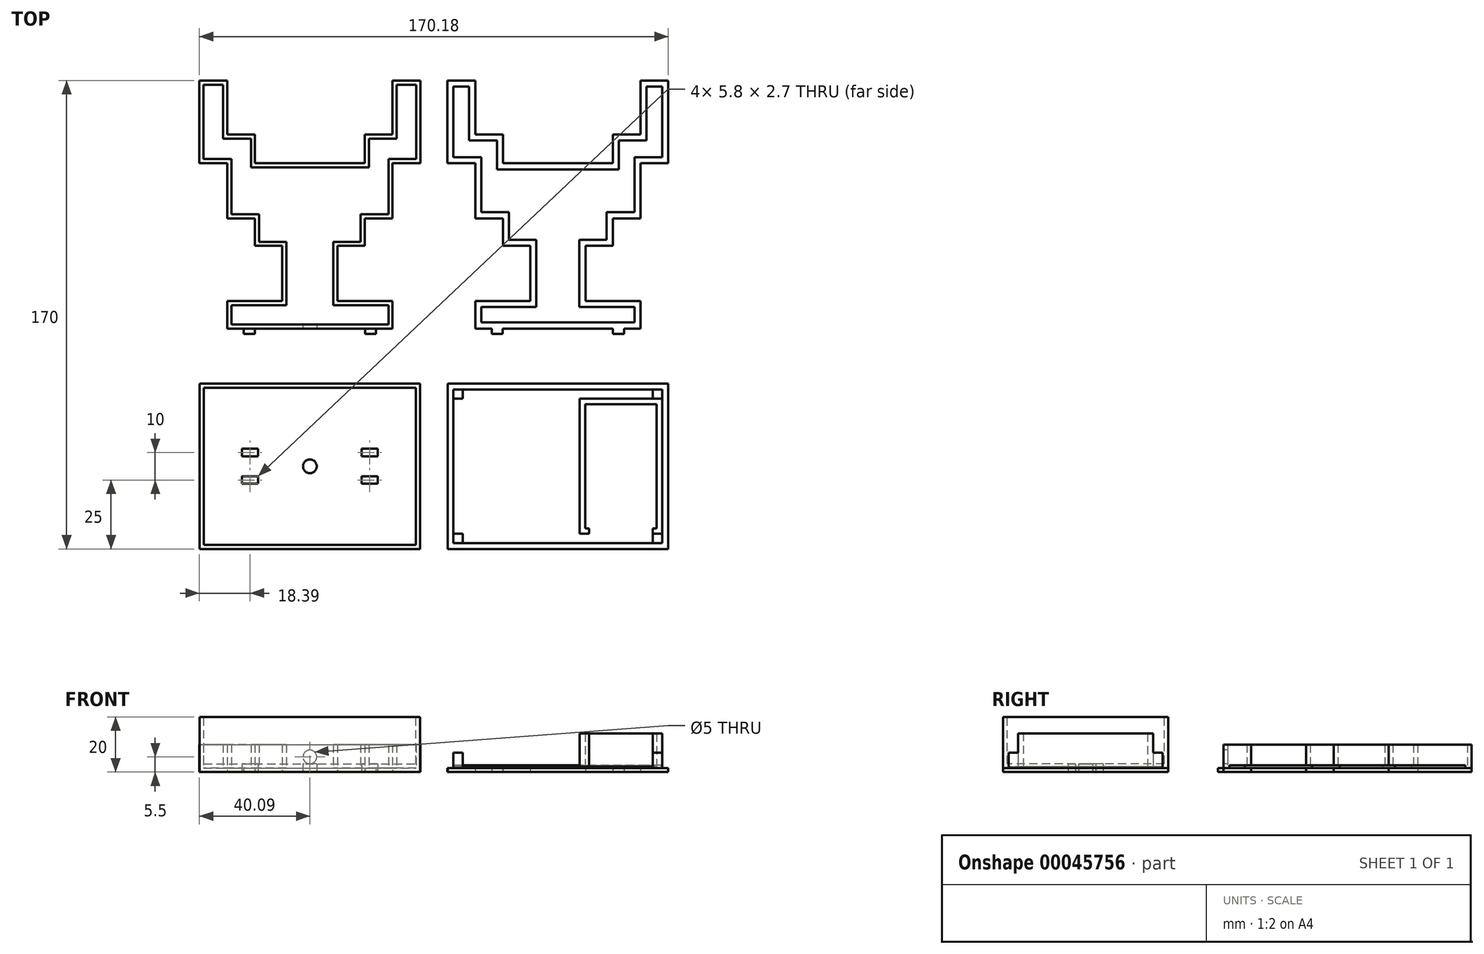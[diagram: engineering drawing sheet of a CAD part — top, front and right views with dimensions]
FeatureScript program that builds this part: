
annotation { "Feature Type Name" : "Feature", "Feature Type Description" : "" }
export const myFeature = defineFeature(function(context is Context, id is Id, definition is map)
    precondition{}
    {
        {
            var Q0;
            Q0=qCreatedBy(makeId("Top.planeOp"),FACE);
            var sketch = newSketch(context, id + "F0", { "sketchPlane" : qUnion([Q0])});
            skLineSegment(sketch, "E0", {"start": v(0, 0) * mm, "end": v(0, 20) * mm, "construction": true});
            skLineSegment(sketch, "E1", {"start": v(0, 0) * mm, "end": v(0, -40) * mm, "construction": true});
            skLineSegment(sketch, "E2", {"start": v(-30, -40) * mm, "end": v(30, -40) * mm});
            skLineSegment(sketch, "E3", {"start": v(-30, -40) * mm, "end": v(-30, -30) * mm});
            skLineSegment(sketch, "E4", {"start": v(-30, -30) * mm, "end": v(-10, -30) * mm});
            skLineSegment(sketch, "E5", {"start": v(-10, -30) * mm, "end": v(-10, -10) * mm});
            skLineSegment(sketch, "E6", {"start": v(-10, -10) * mm, "end": v(-19.9, -10) * mm});
            skLineSegment(sketch, "E7", {"start": v(-19.9, -10) * mm, "end": v(-19.9, 0) * mm});
            skLineSegment(sketch, "E8", {"start": v(-19.9, 0) * mm, "end": v(-30, 0) * mm});
            skLineSegment(sketch, "E9", {"start": v(-19.9, 20) * mm, "end": v(19.9, 20) * mm});
            skLineSegment(sketch, "E10", {"start": v(-19.9, 20) * mm, "end": v(-19.9, 0) * mm, "construction": true});
            skLineSegment(sketch, "E11", {"start": v(-30, 0) * mm, "end": v(-30, 20) * mm});
            skLineSegment(sketch, "E12", {"start": v(-30, 20) * mm, "end": v(-40.1, 20) * mm});
            skLineSegment(sketch, "E13", {"start": v(-40.1, 20) * mm, "end": v(-40.1, 50) * mm});
            skLineSegment(sketch, "E14", {"start": v(-40.1, 50) * mm, "end": v(-30, 50) * mm});
            skLineSegment(sketch, "E15", {"start": v(-30, 50) * mm, "end": v(-30, 30.44) * mm});
            skLineSegment(sketch, "E16", {"start": v(-30, 30.44) * mm, "end": v(-19.9, 30.44) * mm});
            skLineSegment(sketch, "E17", {"start": v(-19.9, 30.44) * mm, "end": v(-19.9, 20) * mm});
            skLineSegment(sketch, "E18.MirrorCS", {"start": v(19.9, 30.44) * mm, "end": v(19.9, 20) * mm});
            skLineSegment(sketch, "E19.MirrorCS", {"start": v(30, 30.44) * mm, "end": v(19.9, 30.44) * mm});
            skLineSegment(sketch, "E20.MirrorCS", {"start": v(30, 50) * mm, "end": v(30, 30.44) * mm});
            skLineSegment(sketch, "E21.MirrorCS", {"start": v(40.1, 50) * mm, "end": v(30, 50) * mm});
            skLineSegment(sketch, "E22.MirrorCS", {"start": v(40.1, 20) * mm, "end": v(40.1, 50) * mm});
            skLineSegment(sketch, "E23.MirrorCS", {"start": v(30, 20) * mm, "end": v(40.1, 20) * mm});
            skLineSegment(sketch, "E24.MirrorCS", {"start": v(30, 0) * mm, "end": v(30, 20) * mm});
            skLineSegment(sketch, "E25.MirrorCS", {"start": v(19.9, 0) * mm, "end": v(30, 0) * mm});
            skLineSegment(sketch, "E26.MirrorCS", {"start": v(19.9, -10) * mm, "end": v(19.9, 0) * mm});
            skLineSegment(sketch, "E27.MirrorCS", {"start": v(10, -10) * mm, "end": v(19.9, -10) * mm});
            skLineSegment(sketch, "E28.MirrorCS", {"start": v(10, -30) * mm, "end": v(10, -10) * mm});
            skLineSegment(sketch, "E29.MirrorCS", {"start": v(30, -30) * mm, "end": v(10, -30) * mm});
            skLineSegment(sketch, "E30.MirrorCS", {"start": v(30, -40) * mm, "end": v(30, -30) * mm});
            skLineSegment(sketch, "E31", {"start": v(0, -42) * mm, "end": v(-20, -42) * mm, "construction": true});
            skLineSegment(sketch, "E32.bottom", {"start": v(-20, -42) * mm, "end": v(-24, -42) * mm});
            skLineSegment(sketch, "E32.top", {"start": v(-20, -40) * mm, "end": v(-24, -40) * mm});
            skLineSegment(sketch, "E32.left", {"start": v(-20, -42) * mm, "end": v(-20, -40) * mm});
            skLineSegment(sketch, "E32.right", {"start": v(-24, -42) * mm, "end": v(-24, -40) * mm});
            skLineSegment(sketch, "E33", {"start": v(0, -40) * mm, "end": v(0, -42) * mm, "construction": true});
            skLineSegment(sketch, "E34.MirrorCS", {"start": v(20, -42) * mm, "end": v(20, -40) * mm});
            skLineSegment(sketch, "E35.MirrorCS", {"start": v(20, -42) * mm, "end": v(24, -42) * mm});
            skLineSegment(sketch, "E36.MirrorCS", {"start": v(24, -42) * mm, "end": v(24, -40) * mm});
            skSolve(sketch);
        }
        {
            var Q0;
            Q0=makeQuery(id+"F0.imprint","IMPRINT",FACE,{"disambiguationData":[TD([[makeQuery(id+"F0.imprint","IMPRINT",EDGE,{"derivedFrom":sQuery(id+"F0.wireOp",EDGE,"E2")}),1.0]])]});
            var Q1;
            Q1=makeQuery(id+"F0.imprint","IMPRINT",FACE,{"disambiguationData":[TD([[makeQuery(id+"F0.imprint","IMPRINT",EDGE,{"derivedFrom":sQuery(id+"F0.wireOp",EDGE,"E32.bottom")}),-1.0]])]});
            var Q2;
            {var subQ1=sQuery(id+"F0.wireOp",EDGE,"E34.MirrorCS");Q2=makeQuery(id+"F0.imprint","IMPRINT",FACE,{"disambiguationData":[TD([[makeQuery(id+"F0.imprint","IMPRINT",EDGE,{"derivedFrom":subQ1}),-1.0]])]});}
            extrude(context, id + "F1", {"entities" : qUnion([Q0, Q1, Q2]), "depth" : 1.5 * mm});
        }
        {
            var Q0;
            Q0=makeQuery(id+"F1.opExtrude","SWEPT_BODY",BODY,{"disambiguationData":[OSD([sQuery(id+"F0.wireOp",EDGE,"E2"),sQuery(id+"F0.wireOp",EDGE,"E3"),sQuery(id+"F0.wireOp",EDGE,"E4"),sQuery(id+"F0.wireOp",EDGE,"E5"),sQuery(id+"F0.wireOp",EDGE,"E6"),sQuery(id+"F0.wireOp",EDGE,"E7"),sQuery(id+"F0.wireOp",EDGE,"E8"),sQuery(id+"F0.wireOp",EDGE,"E9"),sQuery(id+"F0.wireOp",EDGE,"E11"),sQuery(id+"F0.wireOp",EDGE,"E12"),sQuery(id+"F0.wireOp",EDGE,"E13"),sQuery(id+"F0.wireOp",EDGE,"E14"),sQuery(id+"F0.wireOp",EDGE,"E15"),sQuery(id+"F0.wireOp",EDGE,"E16"),sQuery(id+"F0.wireOp",EDGE,"E17"),sQuery(id+"F0.wireOp",EDGE,"E18.MirrorCS"),sQuery(id+"F0.wireOp",EDGE,"E19.MirrorCS"),sQuery(id+"F0.wireOp",EDGE,"E20.MirrorCS"),sQuery(id+"F0.wireOp",EDGE,"E21.MirrorCS"),sQuery(id+"F0.wireOp",EDGE,"E22.MirrorCS"),sQuery(id+"F0.wireOp",EDGE,"E23.MirrorCS"),sQuery(id+"F0.wireOp",EDGE,"E24.MirrorCS"),sQuery(id+"F0.wireOp",EDGE,"E25.MirrorCS"),sQuery(id+"F0.wireOp",EDGE,"E26.MirrorCS"),sQuery(id+"F0.wireOp",EDGE,"E27.MirrorCS"),sQuery(id+"F0.wireOp",EDGE,"E28.MirrorCS"),sQuery(id+"F0.wireOp",EDGE,"E29.MirrorCS"),sQuery(id+"F0.wireOp",EDGE,"E30.MirrorCS")])]});
            transform(context, id + "F2", {"entities" : qUnion([Q0]), "transformType" : TransformType.TRANSLATION_3D, "dx" : 90 * mm, "dy" : 0 * mm, "dz" : 0 * mm, "makeCopy" : true});
        }
        {
            var Q0;
            Q0=makeQuery(id+"F1.opExtrude","CAP_FACE",FACE,{"disambiguationData":[OSD([sQuery(id+"F0.wireOp",EDGE,"E2"),sQuery(id+"F0.wireOp",EDGE,"E3"),sQuery(id+"F0.wireOp",EDGE,"E4"),sQuery(id+"F0.wireOp",EDGE,"E5"),sQuery(id+"F0.wireOp",EDGE,"E6"),sQuery(id+"F0.wireOp",EDGE,"E7"),sQuery(id+"F0.wireOp",EDGE,"E8"),sQuery(id+"F0.wireOp",EDGE,"E9"),sQuery(id+"F0.wireOp",EDGE,"E11"),sQuery(id+"F0.wireOp",EDGE,"E12"),sQuery(id+"F0.wireOp",EDGE,"E13"),sQuery(id+"F0.wireOp",EDGE,"E14"),sQuery(id+"F0.wireOp",EDGE,"E15"),sQuery(id+"F0.wireOp",EDGE,"E16"),sQuery(id+"F0.wireOp",EDGE,"E17"),sQuery(id+"F0.wireOp",EDGE,"E18.MirrorCS"),sQuery(id+"F0.wireOp",EDGE,"E19.MirrorCS"),sQuery(id+"F0.wireOp",EDGE,"E20.MirrorCS"),sQuery(id+"F0.wireOp",EDGE,"E21.MirrorCS"),sQuery(id+"F0.wireOp",EDGE,"E22.MirrorCS"),sQuery(id+"F0.wireOp",EDGE,"E23.MirrorCS"),sQuery(id+"F0.wireOp",EDGE,"E24.MirrorCS"),sQuery(id+"F0.wireOp",EDGE,"E25.MirrorCS"),sQuery(id+"F0.wireOp",EDGE,"E26.MirrorCS"),sQuery(id+"F0.wireOp",EDGE,"E27.MirrorCS"),sQuery(id+"F0.wireOp",EDGE,"E28.MirrorCS"),sQuery(id+"F0.wireOp",EDGE,"E29.MirrorCS"),sQuery(id+"F0.wireOp",EDGE,"E30.MirrorCS"),sQuery(id+"F0.wireOp",EDGE,"E32.bottom"),sQuery(id+"F0.wireOp",EDGE,"E32.left"),sQuery(id+"F0.wireOp",EDGE,"E32.right"),sQuery(id+"F0.wireOp",EDGE,"E34.MirrorCS"),sQuery(id+"F0.wireOp",EDGE,"E35.MirrorCS"),sQuery(id+"F0.wireOp",EDGE,"E36.MirrorCS")])],"isStart":false});
            var sketch = newSketch(context, id + "F3", { "sketchPlane" : qUnion([Q0])});
            skLineSegment(sketch, "E37.0", {"start": v(-30, -40) * mm, "end": v(-30, -30) * mm});
            skLineSegment(sketch, "E38.0", {"start": v(-30, -30) * mm, "end": v(-10, -30) * mm});
            skLineSegment(sketch, "E39.0", {"start": v(-10, -30) * mm, "end": v(-10, -10) * mm});
            skLineSegment(sketch, "E40.0", {"start": v(-10, -10) * mm, "end": v(-19.9, -10) * mm});
            skLineSegment(sketch, "E41.0", {"start": v(-19.9, -10) * mm, "end": v(-19.9, 0) * mm});
            skLineSegment(sketch, "E42.0", {"start": v(-19.9, 0) * mm, "end": v(-30, 0) * mm});
            skLineSegment(sketch, "E43.0", {"start": v(-30, 0) * mm, "end": v(-30, 20) * mm});
            skLineSegment(sketch, "E44.0", {"start": v(-30, 20) * mm, "end": v(-40.1, 20) * mm});
            skLineSegment(sketch, "E45.0", {"start": v(-40.1, 20) * mm, "end": v(-40.1, 50) * mm});
            skLineSegment(sketch, "E46.0", {"start": v(-40.1, 50) * mm, "end": v(-30, 50) * mm});
            skLineSegment(sketch, "E47.0", {"start": v(-30, 50) * mm, "end": v(-30, 30.44) * mm});
            skLineSegment(sketch, "E48.0", {"start": v(-30, 30.44) * mm, "end": v(-19.9, 30.44) * mm});
            skLineSegment(sketch, "E49.0", {"start": v(-19.9, 30.44) * mm, "end": v(-19.9, 20) * mm});
            skLineSegment(sketch, "E50.0", {"start": v(-19.9, 20) * mm, "end": v(19.9, 20) * mm});
            skLineSegment(sketch, "E51.0", {"start": v(19.9, 30.44) * mm, "end": v(19.9, 20) * mm});
            skLineSegment(sketch, "E52.0", {"start": v(30, 30.44) * mm, "end": v(19.9, 30.44) * mm});
            skLineSegment(sketch, "E53.0", {"start": v(30, 50) * mm, "end": v(30, 30.44) * mm});
            skLineSegment(sketch, "E54.0", {"start": v(40.1, 50) * mm, "end": v(30, 50) * mm});
            skLineSegment(sketch, "E55.0", {"start": v(40.1, 20) * mm, "end": v(40.1, 50) * mm});
            skLineSegment(sketch, "E56.0", {"start": v(30, 20) * mm, "end": v(40.1, 20) * mm});
            skLineSegment(sketch, "E57.0", {"start": v(30, 0) * mm, "end": v(30, 20) * mm});
            skLineSegment(sketch, "E58.0", {"start": v(19.9, 0) * mm, "end": v(30, 0) * mm});
            skLineSegment(sketch, "E59.0", {"start": v(19.9, -10) * mm, "end": v(19.9, 0) * mm});
            skLineSegment(sketch, "E60.0", {"start": v(10, -10) * mm, "end": v(19.9, -10) * mm});
            skLineSegment(sketch, "E61.0", {"start": v(10, -30) * mm, "end": v(10, -10) * mm});
            skLineSegment(sketch, "E62.0", {"start": v(30, -30) * mm, "end": v(10, -30) * mm});
            skLineSegment(sketch, "E63.0", {"start": v(30, -40) * mm, "end": v(30, -30) * mm});
            skLineSegment(sketch, "E64", {"start": v(-30, -40) * mm, "end": v(30, -40) * mm});
            skSolve(sketch);
        }
        {
            var Q0;
            {var subQ5=sQuery(id+"F3.wireOp",EDGE,"E37.0");Q0=makeQuery(id+"F3.imprint","IMPRINT",FACE,{"disambiguationData":[TD([[makeQuery(id+"F3.imprint","IMPRINT",EDGE,{"derivedFrom":subQ5}),-1.0]])]});}
            extrude(context, id + "F4", {"entities" : qUnion([Q0]), "operationType" : NewBodyOperationType.ADD, "depth" : 8.5 * mm});
        }
        {
            var Q0;
            Q0=makeQuery(id+"F4.opExtrude","CAP_FACE",FACE,{"disambiguationData":[OSD([sQuery(id+"F3.wireOp",EDGE,"E37.0"),sQuery(id+"F3.wireOp",EDGE,"E38.0"),sQuery(id+"F3.wireOp",EDGE,"E39.0"),sQuery(id+"F3.wireOp",EDGE,"E40.0"),sQuery(id+"F3.wireOp",EDGE,"E41.0"),sQuery(id+"F3.wireOp",EDGE,"E42.0"),sQuery(id+"F3.wireOp",EDGE,"E43.0"),sQuery(id+"F3.wireOp",EDGE,"E44.0"),sQuery(id+"F3.wireOp",EDGE,"E45.0"),sQuery(id+"F3.wireOp",EDGE,"E46.0"),sQuery(id+"F3.wireOp",EDGE,"E47.0"),sQuery(id+"F3.wireOp",EDGE,"E48.0"),sQuery(id+"F3.wireOp",EDGE,"E49.0"),sQuery(id+"F3.wireOp",EDGE,"E50.0"),sQuery(id+"F3.wireOp",EDGE,"E51.0"),sQuery(id+"F3.wireOp",EDGE,"E52.0"),sQuery(id+"F3.wireOp",EDGE,"E53.0"),sQuery(id+"F3.wireOp",EDGE,"E54.0"),sQuery(id+"F3.wireOp",EDGE,"E55.0"),sQuery(id+"F3.wireOp",EDGE,"E56.0"),sQuery(id+"F3.wireOp",EDGE,"E57.0"),sQuery(id+"F3.wireOp",EDGE,"E58.0"),sQuery(id+"F3.wireOp",EDGE,"E59.0"),sQuery(id+"F3.wireOp",EDGE,"E60.0"),sQuery(id+"F3.wireOp",EDGE,"E61.0"),sQuery(id+"F3.wireOp",EDGE,"E62.0"),sQuery(id+"F3.wireOp",EDGE,"E63.0"),sQuery(id+"F3.wireOp",EDGE,"E64")])],"isStart":false});
            shell(context, id + "F5", {"entities" : qUnion([Q0]), "thickness" : 1.5 * mm});
        }
        {
            var Q0;
            {var subQ0=sQuery(id+"F0.wireOp",EDGE,"E2");Q0=makeQuery(id+"F4.boolean.opBoolean","MERGE",FACE,{"derivedFrom":[makeQuery(id+"F1.opExtrude","SWEPT_FACE",FACE,{"disambiguationData":[OSD([subQ0])]}),makeQuery(id+"F4.opExtrude","SWEPT_FACE",FACE,{"disambiguationData":[OSD([subQ0])]})]});}
            var sketch = newSketch(context, id + "F6", { "sketchPlane" : qUnion([Q0])});
            skLineSegment(sketch, "E65", {"start": v(0, 0) * mm, "end": v(0, 5.5) * mm, "construction": true});
            skLineSegment(sketch, "E66.0", {"start": v(-20, 0) * mm, "end": v(20, 0) * mm, "construction": true});
            skPoint(sketch, "E67", {"position": v(0, 5.5) * mm});
            skSolve(sketch);
        }
        {
            var Q0;
            Q0=sQuery(id+"F6.wireOp",VERTEX,"E67");
            var Q1;
            Q1=makeQuery(id+"F1.opExtrude","SWEPT_BODY",BODY,{"disambiguationData":[OSD([sQuery(id+"F0.wireOp",EDGE,"E2"),sQuery(id+"F0.wireOp",EDGE,"E3"),sQuery(id+"F0.wireOp",EDGE,"E4"),sQuery(id+"F0.wireOp",EDGE,"E5"),sQuery(id+"F0.wireOp",EDGE,"E6"),sQuery(id+"F0.wireOp",EDGE,"E7"),sQuery(id+"F0.wireOp",EDGE,"E8"),sQuery(id+"F0.wireOp",EDGE,"E9"),sQuery(id+"F0.wireOp",EDGE,"E11"),sQuery(id+"F0.wireOp",EDGE,"E12"),sQuery(id+"F0.wireOp",EDGE,"E13"),sQuery(id+"F0.wireOp",EDGE,"E14"),sQuery(id+"F0.wireOp",EDGE,"E15"),sQuery(id+"F0.wireOp",EDGE,"E16"),sQuery(id+"F0.wireOp",EDGE,"E17"),sQuery(id+"F0.wireOp",EDGE,"E18.MirrorCS"),sQuery(id+"F0.wireOp",EDGE,"E19.MirrorCS"),sQuery(id+"F0.wireOp",EDGE,"E20.MirrorCS"),sQuery(id+"F0.wireOp",EDGE,"E21.MirrorCS"),sQuery(id+"F0.wireOp",EDGE,"E22.MirrorCS"),sQuery(id+"F0.wireOp",EDGE,"E23.MirrorCS"),sQuery(id+"F0.wireOp",EDGE,"E24.MirrorCS"),sQuery(id+"F0.wireOp",EDGE,"E25.MirrorCS"),sQuery(id+"F0.wireOp",EDGE,"E26.MirrorCS"),sQuery(id+"F0.wireOp",EDGE,"E27.MirrorCS"),sQuery(id+"F0.wireOp",EDGE,"E28.MirrorCS"),sQuery(id+"F0.wireOp",EDGE,"E29.MirrorCS"),sQuery(id+"F0.wireOp",EDGE,"E30.MirrorCS")])]});
            hole(context, id + "F7", {"style" : HoleStyle.SIMPLE, "holeDiameter" : 5 * mm, "endStyle" : HoleEndStyle.BLIND, "holeDepth" : 20 * mm, "locations" : qUnion([Q0]), "scope" : qUnion([Q1])});
        }
        {
            var Q0;
            Q0=makeQuery(id+"F2.opPattern","COPY",FACE,{"derivedFrom":makeQuery(id+"F1.opExtrude","CAP_FACE",FACE,{"disambiguationData":[OSD([sQuery(id+"F0.wireOp",EDGE,"E2"),sQuery(id+"F0.wireOp",EDGE,"E3"),sQuery(id+"F0.wireOp",EDGE,"E4"),sQuery(id+"F0.wireOp",EDGE,"E5"),sQuery(id+"F0.wireOp",EDGE,"E6"),sQuery(id+"F0.wireOp",EDGE,"E7"),sQuery(id+"F0.wireOp",EDGE,"E8"),sQuery(id+"F0.wireOp",EDGE,"E9"),sQuery(id+"F0.wireOp",EDGE,"E11"),sQuery(id+"F0.wireOp",EDGE,"E12"),sQuery(id+"F0.wireOp",EDGE,"E13"),sQuery(id+"F0.wireOp",EDGE,"E14"),sQuery(id+"F0.wireOp",EDGE,"E15"),sQuery(id+"F0.wireOp",EDGE,"E16"),sQuery(id+"F0.wireOp",EDGE,"E17"),sQuery(id+"F0.wireOp",EDGE,"E18.MirrorCS"),sQuery(id+"F0.wireOp",EDGE,"E19.MirrorCS"),sQuery(id+"F0.wireOp",EDGE,"E20.MirrorCS"),sQuery(id+"F0.wireOp",EDGE,"E21.MirrorCS"),sQuery(id+"F0.wireOp",EDGE,"E22.MirrorCS"),sQuery(id+"F0.wireOp",EDGE,"E23.MirrorCS"),sQuery(id+"F0.wireOp",EDGE,"E24.MirrorCS"),sQuery(id+"F0.wireOp",EDGE,"E25.MirrorCS"),sQuery(id+"F0.wireOp",EDGE,"E26.MirrorCS"),sQuery(id+"F0.wireOp",EDGE,"E27.MirrorCS"),sQuery(id+"F0.wireOp",EDGE,"E28.MirrorCS"),sQuery(id+"F0.wireOp",EDGE,"E29.MirrorCS"),sQuery(id+"F0.wireOp",EDGE,"E30.MirrorCS")])],"isStart":false}),"instanceName":"1"});
            var sketch = newSketch(context, id + "F8", { "sketchPlane" : qUnion([Q0])});
            skLineSegment(sketch, "E68.0", {"start": v(62.2, -37.8) * mm, "end": v(62.2, -32.2) * mm});
            skLineSegment(sketch, "E68.1", {"start": v(62.2, -32.2) * mm, "end": v(82.2, -32.2) * mm});
            skLineSegment(sketch, "E68.2", {"start": v(82.2, -32.2) * mm, "end": v(82.2, -7.8) * mm});
            skLineSegment(sketch, "E68.3", {"start": v(82.2, -7.8) * mm, "end": v(72.3, -7.8) * mm});
            skLineSegment(sketch, "E68.4", {"start": v(72.3, -7.8) * mm, "end": v(72.3, 2.2) * mm});
            skLineSegment(sketch, "E68.5", {"start": v(127.9, 47.8) * mm, "end": v(122.2, 47.8) * mm});
            skLineSegment(sketch, "E68.6", {"start": v(127.9, 22.2) * mm, "end": v(127.9, 47.8) * mm});
            skLineSegment(sketch, "E68.7", {"start": v(117.8, 22.2) * mm, "end": v(127.9, 22.2) * mm});
            skLineSegment(sketch, "E68.8", {"start": v(117.8, 2.2) * mm, "end": v(117.8, 22.2) * mm});
            skLineSegment(sketch, "E68.9", {"start": v(107.7, 2.2) * mm, "end": v(117.8, 2.2) * mm});
            skLineSegment(sketch, "E68.10", {"start": v(107.7, -7.8) * mm, "end": v(107.7, 2.2) * mm});
            skLineSegment(sketch, "E68.11", {"start": v(117.8, -37.8) * mm, "end": v(117.8, -32.2) * mm});
            skLineSegment(sketch, "E68.12", {"start": v(117.8, -32.2) * mm, "end": v(97.8, -32.2) * mm});
            skLineSegment(sketch, "E68.13", {"start": v(97.8, -32.2) * mm, "end": v(97.8, -7.8) * mm});
            skLineSegment(sketch, "E68.14", {"start": v(97.8, -7.8) * mm, "end": v(107.7, -7.8) * mm});
            skLineSegment(sketch, "E68.15", {"start": v(122.2, 47.8) * mm, "end": v(122.2, 28.24) * mm});
            skLineSegment(sketch, "E68.16", {"start": v(122.2, 28.24) * mm, "end": v(112.1, 28.24) * mm});
            skLineSegment(sketch, "E68.17", {"start": v(112.1, 28.24) * mm, "end": v(112.1, 17.8) * mm});
            skLineSegment(sketch, "E68.18", {"start": v(67.9, 17.8) * mm, "end": v(112.1, 17.8) * mm});
            skLineSegment(sketch, "E68.19", {"start": v(67.9, 28.24) * mm, "end": v(67.9, 17.8) * mm});
            skLineSegment(sketch, "E68.20", {"start": v(62.2, -37.8) * mm, "end": v(117.8, -37.8) * mm});
            skLineSegment(sketch, "E68.21", {"start": v(57.8, 28.24) * mm, "end": v(67.9, 28.24) * mm});
            skLineSegment(sketch, "E68.22", {"start": v(57.8, 47.8) * mm, "end": v(57.8, 28.24) * mm});
            skLineSegment(sketch, "E68.23", {"start": v(52.1, 47.8) * mm, "end": v(57.8, 47.8) * mm});
            skLineSegment(sketch, "E68.24", {"start": v(52.1, 22.2) * mm, "end": v(52.1, 47.8) * mm});
            skLineSegment(sketch, "E68.25", {"start": v(62.2, 22.2) * mm, "end": v(52.1, 22.2) * mm});
            skLineSegment(sketch, "E68.26", {"start": v(62.2, 2.2) * mm, "end": v(62.2, 22.2) * mm});
            skLineSegment(sketch, "E68.27", {"start": v(72.3, 2.2) * mm, "end": v(62.2, 2.2) * mm});
            skSolve(sketch);
        }
        {
            var Q0;
            Q0 = qSketchRegion(id + "F8", true);
            extrude(context, id + "F9", {"entities" : qUnion([Q0]), "operationType" : NewBodyOperationType.ADD, "depth" : 1 * mm});
        }
        {
            var Q0;
            Q0=qCreatedBy(makeId("Top.planeOp"),FACE);
            var sketch = newSketch(context, id + "F10", { "sketchPlane" : qUnion([Q0])});
            skLineSegment(sketch, "E69", {"start": v(0, 0) * mm, "end": v(0, -90) * mm, "construction": true});
            skLineSegment(sketch, "E70.rect.bottom", {"start": v(-40, -60) * mm, "end": v(40, -60) * mm});
            skLineSegment(sketch, "E70.rect.top", {"start": v(-40, -120) * mm, "end": v(40, -120) * mm});
            skLineSegment(sketch, "E70.rect.left", {"start": v(-40, -60) * mm, "end": v(-40, -120) * mm});
            skLineSegment(sketch, "E70.rect.right", {"start": v(40, -60) * mm, "end": v(40, -120) * mm});
            skPoint(sketch, "E70.rect.middle", {"position": v(0, -90) * mm});
            skCircle(sketch, "E71", {"center": v(0, -90) * mm, "radius": 2.5 * mm});
            skPoint(sketch, "E72.0", {"position": v(-20, -42) * mm});
            skPoint(sketch, "E73.0", {"position": v(-24, -42) * mm});
            skLineSegment(sketch, "E74", {"start": v(-19.4, -85.75) * mm, "end": v(-24, -85.75) * mm, "construction": true});
            skLineSegment(sketch, "E75", {"start": v(-24, -85.75) * mm, "end": v(-24, -84.25) * mm, "construction": true});
            skLineSegment(sketch, "E76", {"start": v(-24, -84.25) * mm, "end": v(-19.4, -84.25) * mm, "construction": true});
            skLineSegment(sketch, "E77", {"start": v(-19.4, -84.25) * mm, "end": v(-19.4, -85.75) * mm, "construction": true});
            skLineSegment(sketch, "E78.0", {"start": v(-24.6, -83.65) * mm, "end": v(-18.8, -83.65) * mm});
            skLineSegment(sketch, "E78.1", {"start": v(-24.6, -86.35) * mm, "end": v(-24.6, -83.65) * mm});
            skLineSegment(sketch, "E78.2", {"start": v(-18.8, -86.35) * mm, "end": v(-24.6, -86.35) * mm});
            skLineSegment(sketch, "E78.3", {"start": v(-18.8, -83.65) * mm, "end": v(-18.8, -86.35) * mm});
            skLineSegment(sketch, "E79", {"start": v(0, -90) * mm, "end": v(-21.7, -90) * mm, "construction": true});
            skLineSegment(sketch, "E80", {"start": v(-21.7, -90) * mm, "end": v(-21.7, -85.75) * mm, "construction": true});
            skLineSegment(sketch, "E81.MirrorCS", {"start": v(-18.8, -93.65) * mm, "end": v(-24.6, -93.65) * mm});
            skLineSegment(sketch, "E82.MirrorCS", {"start": v(-18.8, -96.35) * mm, "end": v(-18.8, -93.65) * mm});
            skLineSegment(sketch, "E83.MirrorCS", {"start": v(-24.6, -96.35) * mm, "end": v(-18.8, -96.35) * mm});
            skLineSegment(sketch, "E84.MirrorCS", {"start": v(-24.6, -93.65) * mm, "end": v(-24.6, -96.35) * mm});
            skLineSegment(sketch, "E85.MirrorCS", {"start": v(18.8, -83.65) * mm, "end": v(18.8, -86.35) * mm});
            skLineSegment(sketch, "E86.MirrorCS", {"start": v(24.6, -83.65) * mm, "end": v(18.8, -83.65) * mm});
            skLineSegment(sketch, "E87.MirrorCS", {"start": v(24.6, -86.35) * mm, "end": v(24.6, -83.65) * mm});
            skLineSegment(sketch, "E88.MirrorCS", {"start": v(18.8, -86.35) * mm, "end": v(24.6, -86.35) * mm});
            skLineSegment(sketch, "E89.MirrorCS", {"start": v(24.6, -93.65) * mm, "end": v(24.6, -96.35) * mm});
            skLineSegment(sketch, "E90.MirrorCS", {"start": v(18.8, -96.35) * mm, "end": v(18.8, -93.65) * mm});
            skLineSegment(sketch, "E91.MirrorCS", {"start": v(18.8, -93.65) * mm, "end": v(24.6, -93.65) * mm});
            skLineSegment(sketch, "E92.MirrorCS", {"start": v(24.6, -96.35) * mm, "end": v(18.8, -96.35) * mm});
            skSolve(sketch);
        }
        {
            var Q0;
            Q0=makeQuery(id+"F10.imprint","IMPRINT",FACE,{"disambiguationData":[TD([[makeQuery(id+"F10.imprint","IMPRINT",EDGE,{"derivedFrom":sQuery(id+"F10.wireOp",EDGE,"E70.rect.bottom")}),-1.0]])]});
            extrude(context, id + "F11", {"entities" : qUnion([Q0]), "depth" : 20 * mm});
        }
        {
            var Q0;
            Q0=makeQuery(id+"F11.opExtrude","CAP_FACE",FACE,{"disambiguationData":[OSD([sQuery(id+"F10.wireOp",EDGE,"E70.rect.bottom"),sQuery(id+"F10.wireOp",EDGE,"E70.rect.top"),sQuery(id+"F10.wireOp",EDGE,"E70.rect.left"),sQuery(id+"F10.wireOp",EDGE,"E70.rect.right"),sQuery(id+"F10.wireOp",EDGE,"E71"),sQuery(id+"F10.wireOp",EDGE,"E78.0"),sQuery(id+"F10.wireOp",EDGE,"E78.1"),sQuery(id+"F10.wireOp",EDGE,"E78.2"),sQuery(id+"F10.wireOp",EDGE,"E78.3"),sQuery(id+"F10.wireOp",EDGE,"E81.MirrorCS"),sQuery(id+"F10.wireOp",EDGE,"E82.MirrorCS"),sQuery(id+"F10.wireOp",EDGE,"E83.MirrorCS"),sQuery(id+"F10.wireOp",EDGE,"E84.MirrorCS"),sQuery(id+"F10.wireOp",EDGE,"E85.MirrorCS"),sQuery(id+"F10.wireOp",EDGE,"E86.MirrorCS"),sQuery(id+"F10.wireOp",EDGE,"E87.MirrorCS"),sQuery(id+"F10.wireOp",EDGE,"E88.MirrorCS"),sQuery(id+"F10.wireOp",EDGE,"E89.MirrorCS"),sQuery(id+"F10.wireOp",EDGE,"E90.MirrorCS"),sQuery(id+"F10.wireOp",EDGE,"E91.MirrorCS"),sQuery(id+"F10.wireOp",EDGE,"E92.MirrorCS")])],"isStart":false});
            var sketch = newSketch(context, id + "F12", { "sketchPlane" : qUnion([Q0])});
            skLineSegment(sketch, "E93.0", {"start": v(-38.5, -61.5) * mm, "end": v(-38.5, -118.5) * mm});
            skLineSegment(sketch, "E93.1", {"start": v(-38.5, -61.5) * mm, "end": v(38.5, -61.5) * mm});
            skLineSegment(sketch, "E93.2", {"start": v(38.5, -61.5) * mm, "end": v(38.5, -118.5) * mm});
            skLineSegment(sketch, "E93.3", {"start": v(-38.5, -118.5) * mm, "end": v(38.5, -118.5) * mm});
            skSolve(sketch);
        }
        {
            var Q0;
            Q0 = qSketchRegion(id + "F12", true);
            extrude(context, id + "F13", {"entities" : qUnion([Q0]), "operationType" : NewBodyOperationType.REMOVE, "oppositeDirection" : true, "depth" : 18.5 * mm});
        }
        {
            var Q0;
            Q0=qCreatedBy(makeId("Top.planeOp"),FACE);
            var sketch = newSketch(context, id + "F14", { "sketchPlane" : qUnion([Q0])});
            skCircle(sketch, "E94.0", {"center": v(0, -90) * mm, "radius": 2.5 * mm, "construction": true});
            skLineSegment(sketch, "E95", {"start": v(0, -90) * mm, "end": v(90, -90) * mm, "construction": true});
            skLineSegment(sketch, "E96.rect.bottom", {"start": v(50, -60) * mm, "end": v(130, -60) * mm});
            skLineSegment(sketch, "E96.rect.top", {"start": v(50, -120) * mm, "end": v(130, -120) * mm});
            skLineSegment(sketch, "E96.rect.left", {"start": v(50, -60) * mm, "end": v(50, -120) * mm});
            skLineSegment(sketch, "E96.rect.right", {"start": v(130, -60) * mm, "end": v(130, -120) * mm});
            skPoint(sketch, "E96.rect.middle", {"position": v(90, -90) * mm});
            skSolve(sketch);
        }
        {
            var Q0;
            {var subQ0=sQuery(id+"F12.wireOp",EDGE,"E93.0");var subQ1=sQuery(id+"F12.wireOp",EDGE,"E93.1");var subQ2=sQuery(id+"F12.wireOp",EDGE,"E93.2");var subQ3=sQuery(id+"F12.wireOp",EDGE,"E93.3");Q0=makeQuery(id+"FpH8dFIfhSpq4S0_2.boolean.opBoolean","SPLIT",FACE,{"disambiguationData":[TD([makeQuery(id+"F11.opExtrude","SWEPT_FACE",FACE,{"disambiguationData":[OSD([sQuery(id+"F10.wireOp",EDGE,"E71")])]})])],"derivedFrom":makeQuery(id+"F13.boolean.opBoolean","COPY",FACE,{"derivedFrom":makeQuery(id+"F13.opExtrude","CAP_FACE",FACE,{"disambiguationData":[OSD([subQ0,subQ1,subQ2,subQ3])],"isStart":false})})});}
            var Q1;
            Q1=makeQuery(id+"F14.imprint","IMPRINT",FACE,{"disambiguationData":[TD([[makeQuery(id+"F14.imprint","IMPRINT",EDGE,{"derivedFrom":sQuery(id+"F14.wireOp",EDGE,"E96.rect.bottom")}),-1.0]])]});
            extrude(context, id + "F15", {"entities" : qUnion([Q0, Q1]), "operationType" : NewBodyOperationType.ADD, "depth" : 1.5 * mm});
        }
        {
            var Q0;
            Q0=makeQuery(id+"F15.opExtrude","CAP_FACE",FACE,{"disambiguationData":[OSD([sQuery(id+"F14.wireOp",EDGE,"E96.rect.bottom"),sQuery(id+"F14.wireOp",EDGE,"E96.rect.top"),sQuery(id+"F14.wireOp",EDGE,"E96.rect.left"),sQuery(id+"F14.wireOp",EDGE,"E96.rect.right")])],"isStart":false});
            var sketch = newSketch(context, id + "F16", { "sketchPlane" : qUnion([Q0])});
            skLineSegment(sketch, "E97.0", {"start": v(52.1, -62.1) * mm, "end": v(127.9, -62.1) * mm});
            skLineSegment(sketch, "E97.1", {"start": v(52.1, -62.1) * mm, "end": v(52.1, -117.9) * mm});
            skLineSegment(sketch, "E97.2", {"start": v(52.1, -117.9) * mm, "end": v(127.9, -117.9) * mm});
            skLineSegment(sketch, "E97.3", {"start": v(127.9, -62.1) * mm, "end": v(127.9, -117.9) * mm});
            skSolve(sketch);
        }
        {
            var Q0;
            Q0 = qSketchRegion(id + "F16", true);
            extrude(context, id + "F17", {"entities" : qUnion([Q0]), "operationType" : NewBodyOperationType.ADD, "depth" : .5 * mm});
        }
        {
            var Q0;
            Q0=makeQuery(id+"F17.opExtrude","CAP_FACE",FACE,{"disambiguationData":[OSD([sQuery(id+"F16.wireOp",EDGE,"E97.0"),sQuery(id+"F16.wireOp",EDGE,"E97.1"),sQuery(id+"F16.wireOp",EDGE,"E97.2"),sQuery(id+"F16.wireOp",EDGE,"E97.3")])],"isStart":false});
            var sketch = newSketch(context, id + "F18", { "sketchPlane" : qUnion([Q0])});
            skLineSegment(sketch, "E98.0", {"start": v(127.9, -62.1) * mm, "end": v(127.9, -117.9) * mm, "construction": true});
            skLineSegment(sketch, "E99.bottom", {"start": v(97.9, -65.5) * mm, "end": v(127.9, -65.5) * mm});
            skLineSegment(sketch, "E99.top", {"start": v(97.9, -114.5) * mm, "end": v(127.9, -114.5) * mm});
            skLineSegment(sketch, "E99.left", {"start": v(97.9, -65.5) * mm, "end": v(97.9, -114.5) * mm});
            skLineSegment(sketch, "E99.right", {"start": v(127.9, -65.5) * mm, "end": v(127.9, -114.5) * mm});
            skPoint(sketch, "E100", {"position": v(127.9, -90) * mm});
            skLineSegment(sketch, "E101.0", {"start": v(99.9, -67.5) * mm, "end": v(125.9, -67.5) * mm});
            skLineSegment(sketch, "E101.1", {"start": v(99.9, -67.5) * mm, "end": v(99.9, -112.5) * mm});
            skLineSegment(sketch, "E101.2", {"start": v(99.9, -112.5) * mm, "end": v(125.9, -112.5) * mm});
            skLineSegment(sketch, "E101.3", {"start": v(125.9, -67.5) * mm, "end": v(125.9, -112.5) * mm});
            skPoint(sketch, "E102.endSnap0", {"position": v(90, -117.9) * mm});
            skSolve(sketch);
        }
        {
            var Q0;
            Q0 = qSketchRegion(id + "F18", true);
            extrude(context, id + "F19", {"entities" : qUnion([Q0]), "operationType" : NewBodyOperationType.ADD, "depth" : 12 * mm});
        }
        {
            var Q0;
            {var subQ0=sQuery(id+"F16.wireOp",EDGE,"E97.0");var subQ1=sQuery(id+"F16.wireOp",EDGE,"E97.1");var subQ2=sQuery(id+"F16.wireOp",EDGE,"E97.2");var subQ3=sQuery(id+"F16.wireOp",EDGE,"E97.3");Q0=makeQuery(id+"F19.boolean.opBoolean","SPLIT",FACE,{"disambiguationData":[TD([makeQuery(id+"F17.opExtrude","SWEPT_FACE",FACE,{"disambiguationData":[OSD([subQ0])]})])],"derivedFrom":makeQuery(id+"F17.opExtrude","CAP_FACE",FACE,{"disambiguationData":[OSD([subQ0,subQ1,subQ2,subQ3])],"isStart":false})});}
            var sketch = newSketch(context, id + "F20", { "sketchPlane" : qUnion([Q0])});
            skLineSegment(sketch, "E103.bottom", {"start": v(127.9, -117.9) * mm, "end": v(124.5, -117.9) * mm});
            skLineSegment(sketch, "E103.top", {"start": v(127.9, -114.5) * mm, "end": v(124.5, -114.5) * mm});
            skLineSegment(sketch, "E103.left", {"start": v(127.9, -117.9) * mm, "end": v(127.9, -114.5) * mm});
            skLineSegment(sketch, "E103.right", {"start": v(124.5, -117.9) * mm, "end": v(124.5, -114.5) * mm});
            skLineSegment(sketch, "E104", {"start": v(90, -62.1) * mm, "end": v(90, -90) * mm, "construction": true});
            skLineSegment(sketch, "E105", {"start": v(90, -90) * mm, "end": v(52.1, -90) * mm, "construction": true});
            skPoint(sketch, "E105.endSnap0", {"position": v(52.1, -90) * mm});
            skLineSegment(sketch, "E106.MirrorCS", {"start": v(124.5, -62.1) * mm, "end": v(124.5, -65.5) * mm});
            skLineSegment(sketch, "E107.MirrorCS", {"start": v(127.9, -65.5) * mm, "end": v(124.5, -65.5) * mm});
            skLineSegment(sketch, "E108.MirrorCS", {"start": v(127.9, -62.1) * mm, "end": v(127.9, -65.5) * mm});
            skLineSegment(sketch, "E109.MirrorCS", {"start": v(127.9, -62.1) * mm, "end": v(124.5, -62.1) * mm});
            skLineSegment(sketch, "E110.MirrorCS", {"start": v(52.1, -65.5) * mm, "end": v(55.5, -65.5) * mm});
            skLineSegment(sketch, "E111.MirrorCS", {"start": v(55.5, -117.9) * mm, "end": v(55.5, -114.5) * mm});
            skLineSegment(sketch, "E112.MirrorCS", {"start": v(52.1, -117.9) * mm, "end": v(52.1, -114.5) * mm});
            skLineSegment(sketch, "E113.MirrorCS", {"start": v(52.1, -114.5) * mm, "end": v(55.5, -114.5) * mm});
            skLineSegment(sketch, "E114.MirrorCS", {"start": v(52.1, -117.9) * mm, "end": v(55.5, -117.9) * mm});
            skLineSegment(sketch, "E115.MirrorCS", {"start": v(55.5, -62.1) * mm, "end": v(55.5, -65.5) * mm});
            skLineSegment(sketch, "E116.MirrorCS", {"start": v(52.1, -62.1) * mm, "end": v(55.5, -62.1) * mm});
            skLineSegment(sketch, "E117.MirrorCS", {"start": v(52.1, -62.1) * mm, "end": v(52.1, -65.5) * mm});
            skSolve(sketch);
        }
        {
            var Q0;
            Q0=makeQuery(id+"F19.opExtrude","CAP_FACE",FACE,{"disambiguationData":[OSD([sQuery(id+"F18.wireOp",EDGE,"E99.bottom"),sQuery(id+"F18.wireOp",EDGE,"E99.top"),sQuery(id+"F18.wireOp",EDGE,"E99.left"),sQuery(id+"F18.wireOp",EDGE,"E99.right"),sQuery(id+"F18.wireOp",EDGE,"E101.0"),sQuery(id+"F18.wireOp",EDGE,"E101.1"),sQuery(id+"F18.wireOp",EDGE,"E101.2"),sQuery(id+"F18.wireOp",EDGE,"E101.3")])],"isStart":false});
            var sketch = newSketch(context, id + "F21", { "sketchPlane" : qUnion([Q0])});
            skLineSegment(sketch, "E118.bottom", {"start": v(101.3, -112.5) * mm, "end": v(124.5, -112.5) * mm});
            skLineSegment(sketch, "E118.top", {"start": v(101.3, -114.5) * mm, "end": v(124.5, -114.5) * mm});
            skLineSegment(sketch, "E118.left", {"start": v(101.3, -112.5) * mm, "end": v(101.3, -114.5) * mm});
            skLineSegment(sketch, "E118.right", {"start": v(124.5, -112.5) * mm, "end": v(124.5, -114.5) * mm});
            skPoint(sketch, "E119", {"position": v(112.9, -114.5) * mm});
            skPoint(sketch, "E120.0", {"position": v(124.5, -114.5) * mm});
            skSolve(sketch);
        }
        {
            var Q0;
            Q0=makeQuery(id+"F21.imprint","IMPRINT",FACE,{"disambiguationData":[TD([[makeQuery(id+"F21.imprint","IMPRINT",EDGE,{"derivedFrom":sQuery(id+"F21.wireOp",EDGE,"E118.bottom")}),-1.0]])]});
            extrude(context, id + "F22", {"entities" : qUnion([Q0]), "operationType" : NewBodyOperationType.REMOVE, "oppositeDirection" : true, "depth" : 12 * mm});
        }
        {
            var Q0;
            Q0 = qSketchRegion(id + "F20", true);
            extrude(context, id + "F23", {"entities" : qUnion([Q0]), "operationType" : NewBodyOperationType.ADD, "depth" : 5 * mm});
        }
    });
